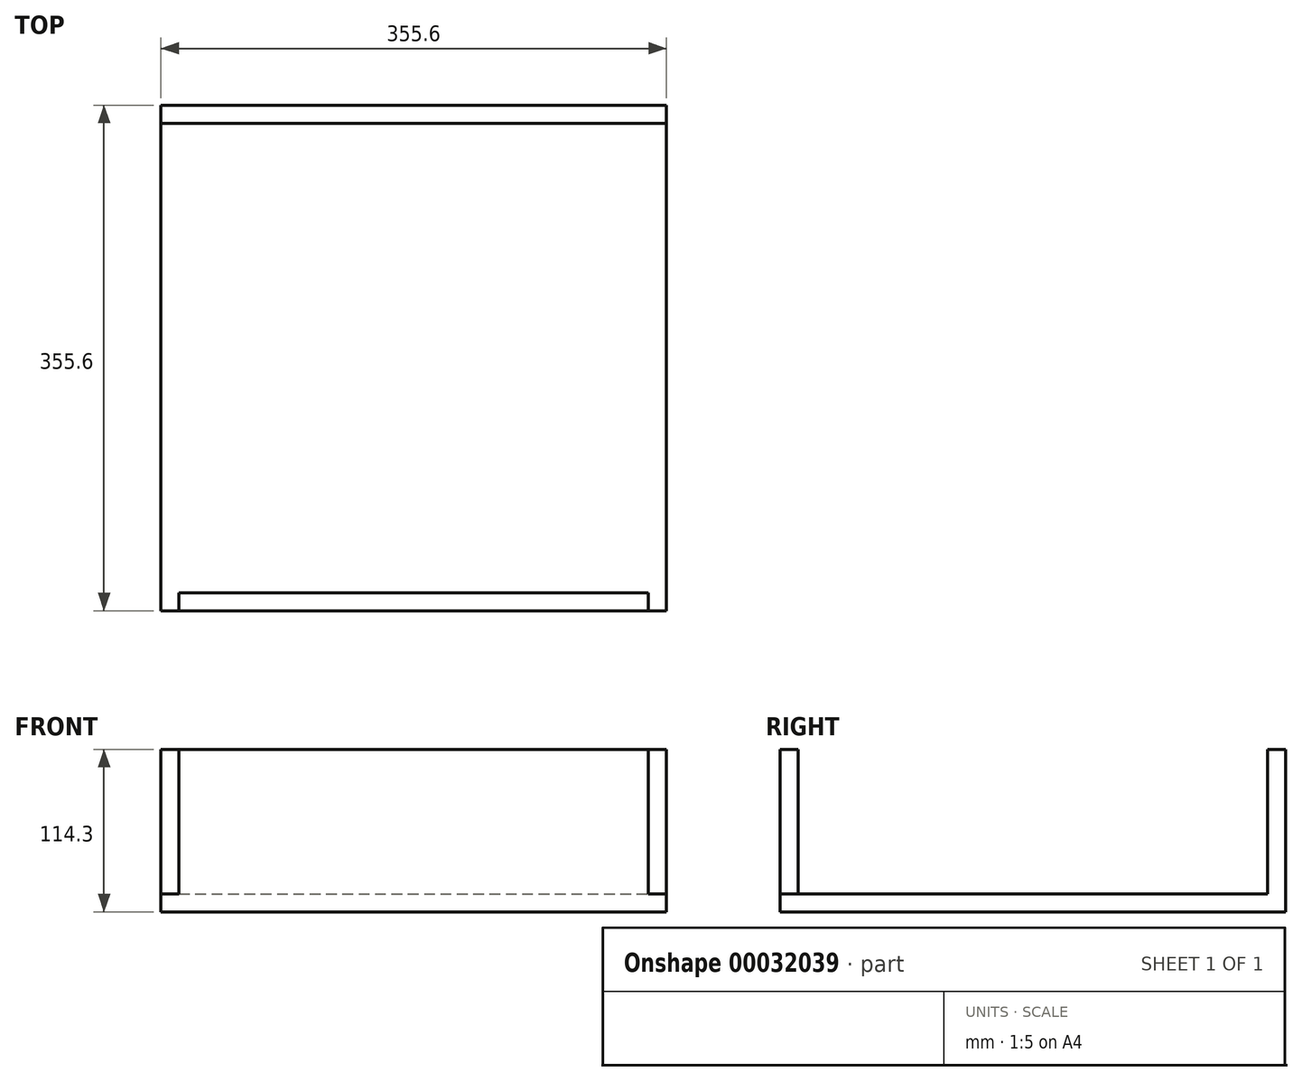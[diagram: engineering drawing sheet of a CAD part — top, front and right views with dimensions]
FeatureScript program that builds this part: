
annotation { "Feature Type Name" : "Feature", "Feature Type Description" : "" }
export const myFeature = defineFeature(function(context is Context, id is Id, definition is map)
    precondition{}
    {
        {
            var Q0;
            Q0=qCreatedBy(makeId("Top.planeOp"),FACE);
            var sketch = newSketch(context, id + "F0", { "sketchPlane" : qUnion([Q0])});
            skLineSegment(sketch, "E0.rect.bottom", {"start": v(177.8, 177.8) * mm, "end": v(-177.8, 177.8) * mm});
            skLineSegment(sketch, "E0.rect.top", {"start": v(177.8, -177.8) * mm, "end": v(-177.8, -177.8) * mm});
            skLineSegment(sketch, "E0.rect.left", {"start": v(177.8, 177.8) * mm, "end": v(177.8, -177.8) * mm});
            skLineSegment(sketch, "E0.rect.right", {"start": v(-177.8, 177.8) * mm, "end": v(-177.8, -177.8) * mm});
            skPoint(sketch, "E0.rect.middle", {"position": v(0, 0) * mm});
            skSolve(sketch);
        }
        {
            var Q0;
            Q0=makeQuery(id+"F0.imprint","IMPRINT",FACE,{"disambiguationData":[TD([[makeQuery(id+"F0.imprint","IMPRINT",EDGE,{"derivedFrom":sQuery(id+"F0.wireOp",EDGE,"E0.rect.bottom")}),1.0]])]});
            extrude(context, id + "F1", {"entities" : qUnion([Q0]), "depth" : 12.7 * mm});
        }
        {
            var Q0;
            Q0=makeQuery(id+"F1.opExtrude","CAP_FACE",FACE,{"disambiguationData":[OSD([sQuery(id+"F0.wireOp",EDGE,"E0.rect.bottom"),sQuery(id+"F0.wireOp",EDGE,"E0.rect.top"),sQuery(id+"F0.wireOp",EDGE,"E0.rect.left"),sQuery(id+"F0.wireOp",EDGE,"E0.rect.right")])],"isStart":false});
            var sketch = newSketch(context, id + "F2", { "sketchPlane" : qUnion([Q0])});
            skLineSegment(sketch, "E1", {"start": v(177.8, 177.8) * mm, "end": v(177.8, 165.1) * mm});
            skLineSegment(sketch, "E2.bottom", {"start": v(177.8, 165.1) * mm, "end": v(-177.8, 165.1) * mm});
            skLineSegment(sketch, "E2.top", {"start": v(177.8, 177.8) * mm, "end": v(-177.8, 177.8) * mm});
            skLineSegment(sketch, "E2.left", {"start": v(177.8, 165.1) * mm, "end": v(177.8, 177.8) * mm});
            skLineSegment(sketch, "E2.right", {"start": v(-177.8, 165.1) * mm, "end": v(-177.8, 177.8) * mm});
            skSolve(sketch);
        }
        {
            var Q0;
            Q0=makeQuery(id+"F1.opExtrude","CAP_FACE",FACE,{"disambiguationData":[OSD([sQuery(id+"F0.wireOp",EDGE,"E0.rect.bottom"),sQuery(id+"F0.wireOp",EDGE,"E0.rect.top"),sQuery(id+"F0.wireOp",EDGE,"E0.rect.left"),sQuery(id+"F0.wireOp",EDGE,"E0.rect.right")])],"isStart":false});
            var sketch = newSketch(context, id + "F3", { "sketchPlane" : qUnion([Q0])});
            skLineSegment(sketch, "E3", {"start": v(177.8, 165.1) * mm, "end": v(165.1, 165.1) * mm});
            skLineSegment(sketch, "E4.bottom", {"start": v(165.1, 165.1) * mm, "end": v(177.8, 165.1) * mm});
            skLineSegment(sketch, "E4.top", {"start": v(165.1, -177.8) * mm, "end": v(177.8, -177.8) * mm});
            skLineSegment(sketch, "E4.left", {"start": v(165.1, 165.1) * mm, "end": v(165.1, -177.8) * mm});
            skLineSegment(sketch, "E4.right", {"start": v(177.8, 165.1) * mm, "end": v(177.8, -177.8) * mm});
            skLineSegment(sketch, "E5", {"start": v(-177.8, -177.8) * mm, "end": v(-177.8, -165.1) * mm});
            skLineSegment(sketch, "E6.right", {"start": v(165.1, -165.1) * mm, "end": v(165.1, -177.8) * mm});
            skLineSegment(sketch, "E7", {"start": v(-177.8, -177.8) * mm, "end": v(-165.1, -177.8) * mm});
            skLineSegment(sketch, "E8.bottom", {"start": v(-165.1, -177.8) * mm, "end": v(-177.8, -177.8) * mm});
            skLineSegment(sketch, "E8.top", {"start": v(-165.1, 177.8) * mm, "end": v(-177.8, 177.8) * mm});
            skLineSegment(sketch, "E8.left", {"start": v(-165.1, -177.8) * mm, "end": v(-165.1, 177.8) * mm});
            skLineSegment(sketch, "E8.right", {"start": v(-177.8, -177.8) * mm, "end": v(-177.8, 177.8) * mm});
            skSolve(sketch);
        }
        {
            var Q0;
            Q0=makeQuery(id+"F2.imprint","IMPRINT",FACE,{"disambiguationData":[TD([[makeQuery(id+"F2.imprint","IMPRINT",EDGE,{"derivedFrom":sQuery(id+"F2.wireOp",EDGE,"E2.bottom")}),-1.0]])]});
            var Q1;
            {var subQ1=sQuery(id+"F3.wireOp",EDGE,"E8.bottom");Q1=makeQuery(id+"F3.imprint","IMPRINT",FACE,{"disambiguationData":[TD([[makeQuery(id+"F3.imprint","IMPRINT",EDGE,{"derivedFrom":subQ1}),-1.0]])]});}
            var Q2;
            Q2=makeQuery(id+"F3.imprint","IMPRINT",FACE,{"disambiguationData":[TD([[makeQuery(id+"F3.imprint","IMPRINT",EDGE,{"derivedFrom":sQuery(id+"F3.wireOp",EDGE,"E4.bottom")}),-1.0]])]});
            extrude(context, id + "F4", {"entities" : qUnion([Q0, Q1, Q2]), "operationType" : NewBodyOperationType.ADD, "depth" : 101.6 * mm});
        }
        {
            var Q0;
            Q0=makeQuery(id+"F1.opExtrude","CAP_FACE",FACE,{"disambiguationData":[OSD([sQuery(id+"F0.wireOp",EDGE,"E0.rect.bottom"),sQuery(id+"F0.wireOp",EDGE,"E0.rect.top"),sQuery(id+"F0.wireOp",EDGE,"E0.rect.left"),sQuery(id+"F0.wireOp",EDGE,"E0.rect.right")])],"isStart":false});
            var sketch = newSketch(context, id + "F5", { "sketchPlane" : qUnion([Q0])});
            skLineSegment(sketch, "E9.bottom", {"start": v(-165.1, -177.8) * mm, "end": v(165.1, -177.8) * mm});
            skLineSegment(sketch, "E9.top", {"start": v(-165.1, -165.1) * mm, "end": v(165.1, -165.1) * mm});
            skLineSegment(sketch, "E9.left", {"start": v(-165.1, -177.8) * mm, "end": v(-165.1, -165.1) * mm});
            skLineSegment(sketch, "E9.right", {"start": v(165.1, -177.8) * mm, "end": v(165.1, -165.1) * mm});
            skSolve(sketch);
        }
        {
            var Q0;
            Q0=makeQuery(id+"F5.imprint","IMPRINT",FACE,{"disambiguationData":[TD([[makeQuery(id+"F5.imprint","IMPRINT",EDGE,{"derivedFrom":sQuery(id+"F5.wireOp",EDGE,"E9.bottom")}),-1.0]])]});
            extrude(context, id + "F6", {"entities" : qUnion([Q0]), "operationType" : NewBodyOperationType.ADD, "depth" : 101.6 * mm});
        }
    });
